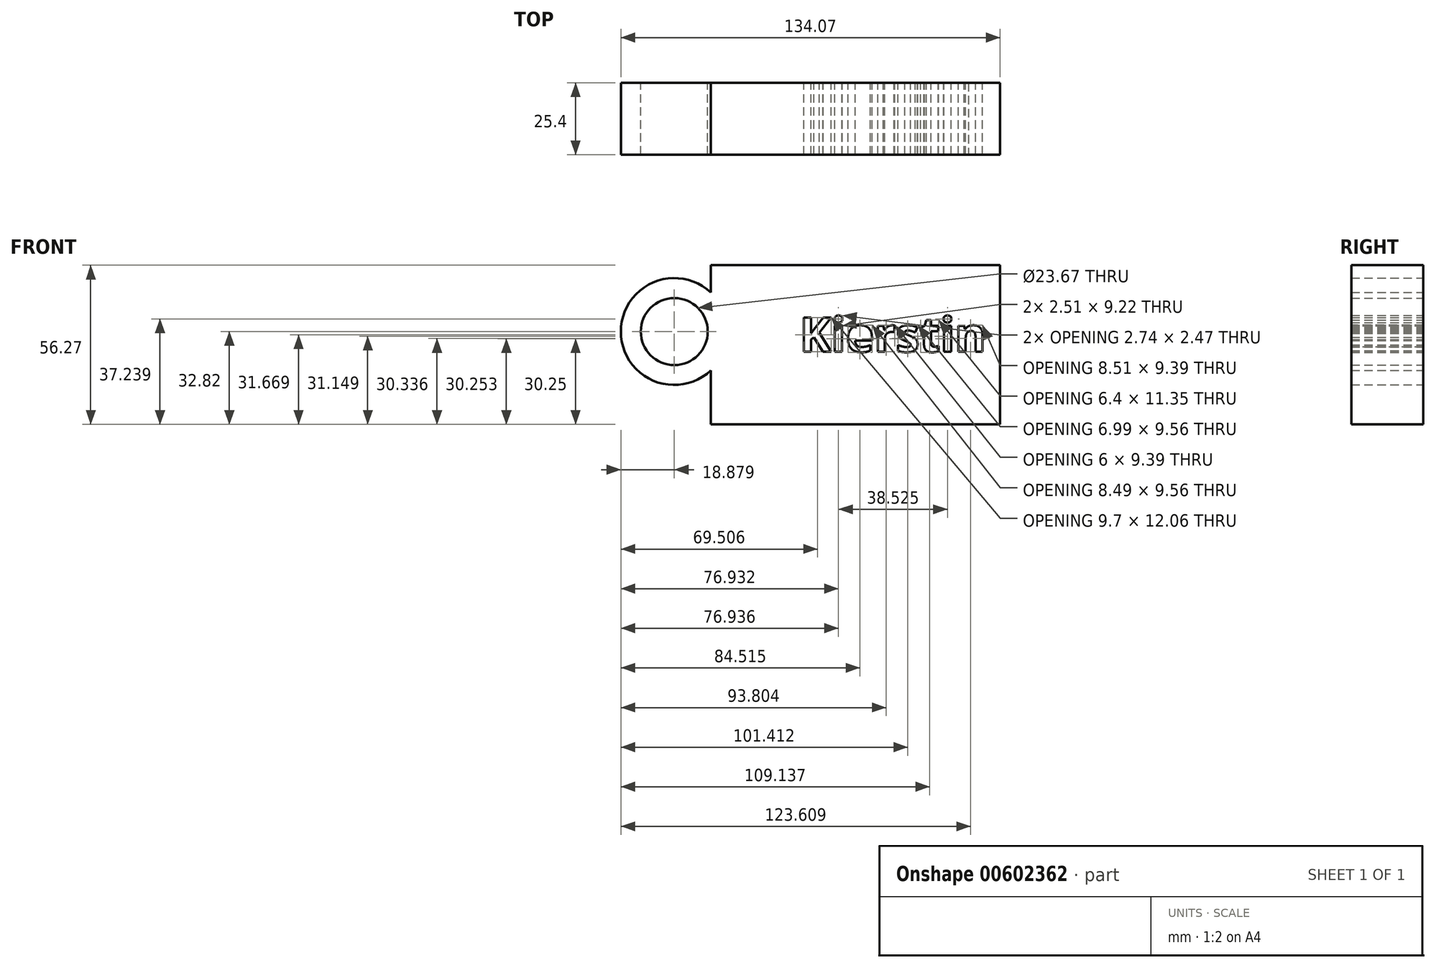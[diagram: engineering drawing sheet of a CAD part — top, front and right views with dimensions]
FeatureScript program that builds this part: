
annotation { "Feature Type Name" : "Feature", "Feature Type Description" : "" }
export const myFeature = defineFeature(function(context is Context, id is Id, definition is map)
    precondition{}
    {
        {
            var Q0;
            Q0=qCreatedBy(makeId("Front.planeOp"),FACE);
            var sketch = newSketch(context, id + "F0", { "sketchPlane" : qUnion([Q0])});
            skLineSegment(sketch, "E0.bottom", {"start": v(-58.47, 30.63) * mm, "end": v(43.81, 30.63) * mm});
            skLineSegment(sketch, "E0.top", {"start": v(-58.47, -25.64) * mm, "end": v(43.81, -25.64) * mm});
            skLineSegment(sketch, "E0.left", {"start": v(-58.47, 30.63) * mm, "end": v(-58.47, -25.64) * mm});
            skLineSegment(sketch, "E0.right", {"start": v(43.81, 30.63) * mm, "end": v(43.81, -25.64) * mm});
            skArc(sketch, "E1", {"start": v(-58.47, 20.96) * mm, "mid": v(-90.26, 7.18) * mm, "end": v(-58.47, -6.6) * mm});
            skCircle(sketch, "E2", {"center": v(-71.38, 7.18) * mm, "radius": 11.84 * mm});
            skText(sketch, "E3", { "text": "Kierstin ", "fontName": "OpenSans-Bold.ttf"});
            const initialGuessF0  = {"E3": [-0.02712, 0, 1, 0, 0.01216]};
            skSetInitialGuess(sketch, initialGuessF0);
            skSolve(sketch);
        }
        {
            var Q0;
            Q0 = qSketchRegion(id + "F0", true);
            extrude(context, id + "F1", {"entities" : qUnion([Q0]), "depth" : 25.4 * mm, "offsetDistance" : 25.4 * mm});
        }
    });
